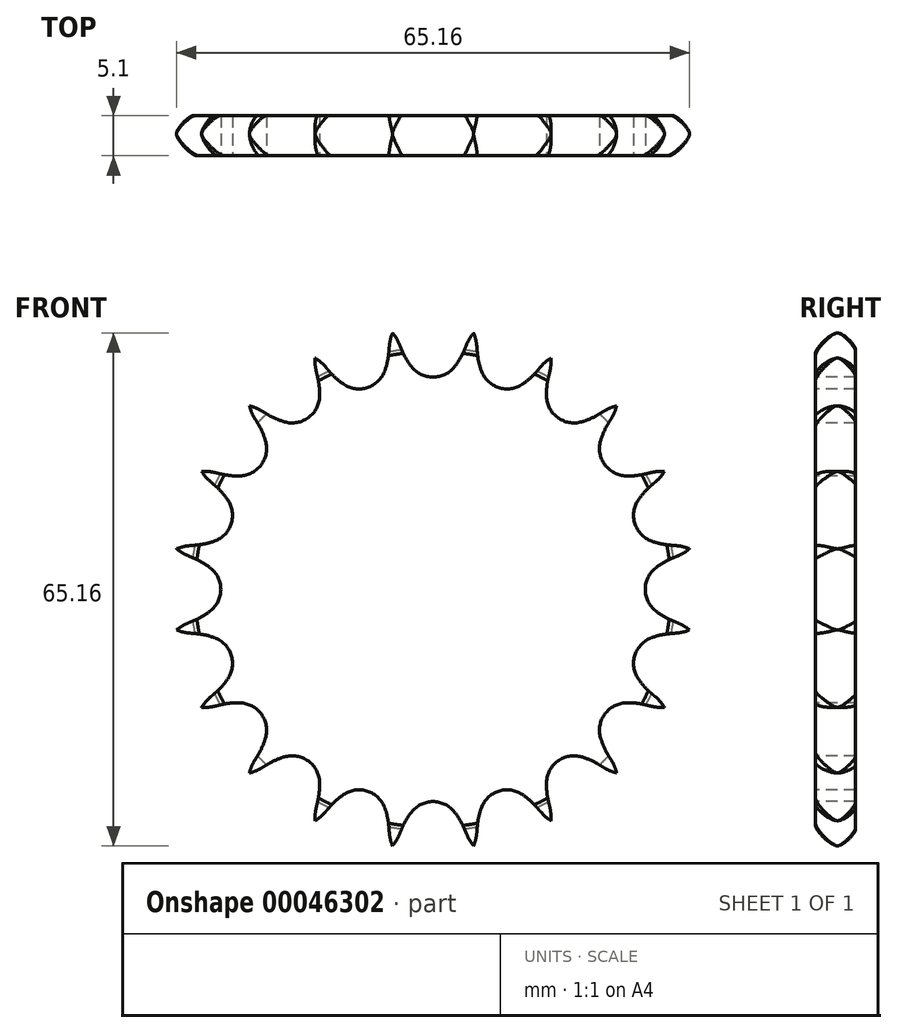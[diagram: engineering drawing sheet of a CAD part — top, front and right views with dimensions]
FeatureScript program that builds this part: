
annotation { "Feature Type Name" : "Feature", "Feature Type Description" : "" }
export const myFeature = defineFeature(function(context is Context, id is Id, definition is map)
    precondition{}
    {
        {
            var Q0;
            Q0=qCreatedBy(makeId("Right.planeOp"),FACE);
            var sketch = newSketch(context, id + "F0", { "sketchPlane" : qUnion([Q0])});
            skLineSegment(sketch, "E0", {"start": v(0, 0) * mm, "end": v(5.1, 0) * mm, "construction": true});
            skLineSegment(sketch, "E1", {"start": v(0, 32.98) * mm, "end": v(5.1, 32.98) * mm});
            skLineSegment(sketch, "E2", {"start": v(5.1, 32.98) * mm, "end": v(5.1, 30) * mm});
            skLineSegment(sketch, "E3", {"start": v(5.1, 30) * mm, "end": v(5.1, 30) * mm});
            skLineSegment(sketch, "E4", {"start": v(5.1, 30) * mm, "end": v(5.1, 0) * mm});
            skLineSegment(sketch, "E5", {"start": v(0, 0) * mm, "end": v(0, 32.98) * mm});
            skLineSegment(sketch, "E6.0.MirrorCS", {"start": v(0, -32.98) * mm, "end": v(5.1, -32.98) * mm});
            skLineSegment(sketch, "E6.1.MirrorCS", {"start": v(5.1, -32.98) * mm, "end": v(5.1, -30) * mm});
            skLineSegment(sketch, "E6.3.MirrorCS", {"start": v(5.1, -30) * mm, "end": v(5.1, 0) * mm});
            skLineSegment(sketch, "E6.4.MirrorCS", {"start": v(5.1, -30) * mm, "end": v(5.1, -30) * mm});
            skLineSegment(sketch, "E6.5.MirrorCS", {"start": v(0, 0) * mm, "end": v(0, -32.98) * mm});
            skLineSegment(sketch, "E7", {"start": v(0, 0) * mm, "end": v(5.1, 0) * mm});
            skLineSegment(sketch, "E8", {"start": v(5.1, 30) * mm, "end": v(0, 30) * mm, "construction": true});
            skLineSegment(sketch, "E9", {"start": v(5.1, -30) * mm, "end": v(0, -30) * mm, "construction": true});
            skSolve(sketch);
        }
        {
            var Q0;
            Q0=makeQuery(id+"F0.imprint","IMPRINT",FACE,{"disambiguationData":[TD([[makeQuery(id+"F0.imprint","IMPRINT",EDGE,{"derivedFrom":sQuery(id+"F0.wireOp",EDGE,"E1")}),-1.0]])]});
            var Q1;
            Q1=sQuery(id+"F0.wireOp",EDGE,"E0");
            revolve(context, id + "F1", {"entities" : qUnion([Q0]), "axis" : qUnion([Q1]), "revolveType" : RevolveType.FULL});
        }
        {
            var Q0;
            Q0=makeQuery(id+"F1.opRevolve","SWEPT_EDGE",EDGE,{"disambiguationData":[OSD([sQuery(id+"F0.wireOp",EDGE,"E1"),sQuery(id+"F0.wireOp",EDGE,"E5")])]});
            fillet(context, id + "F2", {"entities" : qUnion([Q0]), "radius" : 2.75 * mm, "tangentPropagation" : true, "rho" : 0.2, "crossSection" : FilletCrossSection.CONIC, "allowEdgeOverflow" : false});
        }
        {
            var Q0;
            Q0=makeQuery(id+"F1.opRevolve","SWEPT_EDGE",EDGE,{"disambiguationData":[OSD([sQuery(id+"F0.wireOp",EDGE,"E1"),sQuery(id+"F0.wireOp",EDGE,"E2")])]});
            fillet(context, id + "F3", {"entities" : qUnion([Q0]), "radius" : 2.25 * mm, "tangentPropagation" : true, "rho" : 0.2, "crossSection" : FilletCrossSection.CONIC, "allowEdgeOverflow" : false});
        }
        {
            var Q0;
            Q0=makeQuery(id+"F1.opRevolve","SWEPT_FACE",FACE,{"disambiguationData":[OSD([sQuery(id+"F0.wireOp",EDGE,"E5")])]});
            var sketch = newSketch(context, id + "F4", { "sketchPlane" : qUnion([Q0])});
            skCircle(sketch, "E10", {"center": v(0, 0) * mm, "radius": 30.44 * mm, "construction": true});
            skLineSegment(sketch, "E11", {"start": v(0, 0) * mm, "end": v(0, 30.44) * mm, "construction": true});
            skLineSegment(sketch, "E12", {"start": v(0, 30.44) * mm, "end": v(17.07, 30.44) * mm, "construction": true});
            skLineSegment(sketch, "E13", {"start": v(0, 30.44) * mm, "end": v(4.32, 33.82) * mm, "construction": true});
            skLineSegment(sketch, "E14", {"start": v(4.32, 33.82) * mm, "end": v(-3.95, 30.35) * mm, "construction": true});
            skLineSegment(sketch, "E15", {"start": v(-3.95, 30.35) * mm, "end": v(-4.28, 31.13) * mm});
            skLineSegment(sketch, "E16", {"start": v(0, 0) * mm, "end": v(-5.16, 32.58) * mm, "construction": true});
            skArc(sketch, "E17", {"start": v(-5.16, 32.58) * mm, "mid": v(-14.3, 26) * mm, "end": v(-4.28, 31.13) * mm, "construction": true});
            skArc(sketch, "E18", {"start": v(-4.28, 31.13) * mm, "mid": v(-4.66, 31.89) * mm, "end": v(-5.16, 32.58) * mm});
            skLineSegment(sketch, "E19", {"start": v(-4.28, 31.13) * mm, "end": v(-10.5, 45.96) * mm, "construction": true});
            skArc(sketch, "E20", {"start": v(-3.95, 30.35) * mm, "mid": v(-3.41, 29.28) * mm, "end": v(-2.75, 28.3) * mm});
            skArc(sketch, "E21", {"start": v(-2.75, 28.3) * mm, "mid": v(12.06, 38.36) * mm, "end": v(-3.95, 30.35) * mm, "construction": true});
            skArc(sketch, "E22.0.MirrorCS", {"start": v(3.95, 30.35) * mm, "mid": v(3.41, 29.28) * mm, "end": v(2.75, 28.3) * mm});
            skLineSegment(sketch, "E23.0.MirrorCS", {"start": v(3.95, 30.35) * mm, "end": v(4.28, 31.13) * mm});
            skArc(sketch, "E24.0.MirrorCS", {"start": v(4.28, 31.13) * mm, "mid": v(4.66, 31.89) * mm, "end": v(5.16, 32.58) * mm});
            skArc(sketch, "E25", {"start": v(-2.75, 28.3) * mm, "mid": v(0, 26.96) * mm, "end": v(2.75, 28.3) * mm});
            skArc(sketch, "E26", {"start": v(2.75, 28.3) * mm, "mid": v(0, 33.93) * mm, "end": v(-2.75, 28.3) * mm, "construction": true});
            skLineSegment(sketch, "E27", {"start": v(-49.44, 0) * mm, "end": v(0, 0) * mm, "construction": true});
            skArc(sketch, "E28.1.0", {"start": v(-5.55, 30.93) * mm, "mid": v(-5.42, 31.77) * mm, "end": v(-5.16, 32.58) * mm});
            skLineSegment(sketch, "E28.1.1", {"start": v(-5.62, 30.08) * mm, "end": v(-5.55, 30.93) * mm});
            skArc(sketch, "E28.1.2", {"start": v(-5.62, 30.08) * mm, "mid": v(-5.8, 28.9) * mm, "end": v(-6.13, 27.76) * mm});
            skArc(sketch, "E28.1.3", {"start": v(-11.36, 26.07) * mm, "mid": v(-8.33, 25.64) * mm, "end": v(-6.13, 27.76) * mm});
            skArc(sketch, "E28.1.4", {"start": v(-13.13, 27.64) * mm, "mid": v(-12.3, 26.8) * mm, "end": v(-11.36, 26.07) * mm});
            skLineSegment(sketch, "E28.1.5", {"start": v(-13.13, 27.64) * mm, "end": v(-13.69, 28.29) * mm});
            skArc(sketch, "E28.1.6", {"start": v(-13.69, 28.29) * mm, "mid": v(-14.29, 28.89) * mm, "end": v(-14.97, 29.39) * mm});
            skArc(sketch, "E28.2.0", {"start": v(-14.84, 27.7) * mm, "mid": v(-14.97, 28.54) * mm, "end": v(-14.97, 29.39) * mm});
            skLineSegment(sketch, "E28.2.1", {"start": v(-14.64, 26.87) * mm, "end": v(-14.84, 27.7) * mm});
            skArc(sketch, "E28.2.2", {"start": v(-14.64, 26.87) * mm, "mid": v(-14.45, 25.7) * mm, "end": v(-14.41, 24.5) * mm});
            skArc(sketch, "E28.2.3", {"start": v(-18.85, 21.28) * mm, "mid": v(-15.85, 21.81) * mm, "end": v(-14.41, 24.5) * mm});
            skArc(sketch, "E28.2.4", {"start": v(-21.03, 22.23) * mm, "mid": v(-19.97, 21.68) * mm, "end": v(-18.85, 21.28) * mm});
            skLineSegment(sketch, "E28.2.5", {"start": v(-21.03, 22.23) * mm, "end": v(-21.76, 22.67) * mm});
            skArc(sketch, "E28.2.6", {"start": v(-21.76, 22.67) * mm, "mid": v(-22.52, 23.06) * mm, "end": v(-23.32, 23.32) * mm});
            skArc(sketch, "E28.3.0", {"start": v(-22.67, 21.76) * mm, "mid": v(-23.06, 22.52) * mm, "end": v(-23.32, 23.32) * mm});
            skLineSegment(sketch, "E28.3.1", {"start": v(-22.23, 21.03) * mm, "end": v(-22.67, 21.76) * mm});
            skArc(sketch, "E28.3.2", {"start": v(-22.23, 21.03) * mm, "mid": v(-21.68, 19.97) * mm, "end": v(-21.28, 18.85) * mm});
            skArc(sketch, "E28.3.3", {"start": v(-24.5, 14.41) * mm, "mid": v(-21.81, 15.85) * mm, "end": v(-21.28, 18.85) * mm});
            skArc(sketch, "E28.3.4", {"start": v(-26.87, 14.64) * mm, "mid": v(-25.7, 14.45) * mm, "end": v(-24.5, 14.41) * mm});
            skLineSegment(sketch, "E28.3.5", {"start": v(-26.87, 14.64) * mm, "end": v(-27.7, 14.84) * mm});
            skArc(sketch, "E28.3.6", {"start": v(-27.7, 14.84) * mm, "mid": v(-28.54, 14.97) * mm, "end": v(-29.39, 14.97) * mm});
            skArc(sketch, "E28.4.0", {"start": v(-28.29, 13.69) * mm, "mid": v(-28.89, 14.29) * mm, "end": v(-29.39, 14.97) * mm});
            skLineSegment(sketch, "E28.4.1", {"start": v(-27.64, 13.13) * mm, "end": v(-28.29, 13.69) * mm});
            skArc(sketch, "E28.4.2", {"start": v(-27.64, 13.13) * mm, "mid": v(-26.8, 12.3) * mm, "end": v(-26.07, 11.36) * mm});
            skArc(sketch, "E28.4.3", {"start": v(-27.76, 6.13) * mm, "mid": v(-25.64, 8.33) * mm, "end": v(-26.07, 11.36) * mm});
            skArc(sketch, "E28.4.4", {"start": v(-30.08, 5.62) * mm, "mid": v(-28.9, 5.8) * mm, "end": v(-27.76, 6.13) * mm});
            skLineSegment(sketch, "E28.4.5", {"start": v(-30.08, 5.62) * mm, "end": v(-30.93, 5.55) * mm});
            skArc(sketch, "E28.4.6", {"start": v(-30.93, 5.55) * mm, "mid": v(-31.77, 5.42) * mm, "end": v(-32.58, 5.16) * mm});
            skArc(sketch, "E28.5.0", {"start": v(-31.13, 4.28) * mm, "mid": v(-31.89, 4.66) * mm, "end": v(-32.58, 5.16) * mm});
            skLineSegment(sketch, "E28.5.1", {"start": v(-30.35, 3.95) * mm, "end": v(-31.13, 4.28) * mm});
            skArc(sketch, "E28.5.2", {"start": v(-30.35, 3.95) * mm, "mid": v(-29.28, 3.41) * mm, "end": v(-28.3, 2.75) * mm});
            skArc(sketch, "E28.5.3", {"start": v(-28.3, -2.75) * mm, "mid": v(-26.96, 0) * mm, "end": v(-28.3, 2.75) * mm});
            skArc(sketch, "E28.5.4", {"start": v(-30.35, -3.95) * mm, "mid": v(-29.28, -3.41) * mm, "end": v(-28.3, -2.75) * mm});
            skLineSegment(sketch, "E28.5.5", {"start": v(-30.35, -3.95) * mm, "end": v(-31.13, -4.28) * mm});
            skArc(sketch, "E28.5.6", {"start": v(-31.13, -4.28) * mm, "mid": v(-31.89, -4.66) * mm, "end": v(-32.58, -5.16) * mm});
            skArc(sketch, "E28.6.0", {"start": v(-30.93, -5.55) * mm, "mid": v(-31.77, -5.42) * mm, "end": v(-32.58, -5.16) * mm});
            skLineSegment(sketch, "E28.6.1", {"start": v(-30.08, -5.62) * mm, "end": v(-30.93, -5.55) * mm});
            skArc(sketch, "E28.6.2", {"start": v(-30.08, -5.62) * mm, "mid": v(-28.9, -5.8) * mm, "end": v(-27.76, -6.13) * mm});
            skArc(sketch, "E28.6.3", {"start": v(-26.07, -11.36) * mm, "mid": v(-25.64, -8.33) * mm, "end": v(-27.76, -6.13) * mm});
            skArc(sketch, "E28.6.4", {"start": v(-27.64, -13.13) * mm, "mid": v(-26.8, -12.3) * mm, "end": v(-26.07, -11.36) * mm});
            skLineSegment(sketch, "E28.6.5", {"start": v(-27.64, -13.13) * mm, "end": v(-28.29, -13.69) * mm});
            skArc(sketch, "E28.6.6", {"start": v(-28.29, -13.69) * mm, "mid": v(-28.89, -14.29) * mm, "end": v(-29.39, -14.97) * mm});
            skArc(sketch, "E28.7.0", {"start": v(-27.7, -14.84) * mm, "mid": v(-28.54, -14.97) * mm, "end": v(-29.39, -14.97) * mm});
            skLineSegment(sketch, "E28.7.1", {"start": v(-26.87, -14.64) * mm, "end": v(-27.7, -14.84) * mm});
            skArc(sketch, "E28.7.2", {"start": v(-26.87, -14.64) * mm, "mid": v(-25.7, -14.45) * mm, "end": v(-24.5, -14.41) * mm});
            skArc(sketch, "E28.7.3", {"start": v(-21.28, -18.85) * mm, "mid": v(-21.81, -15.85) * mm, "end": v(-24.5, -14.41) * mm});
            skArc(sketch, "E28.7.4", {"start": v(-22.23, -21.03) * mm, "mid": v(-21.68, -19.97) * mm, "end": v(-21.28, -18.85) * mm});
            skLineSegment(sketch, "E28.7.5", {"start": v(-22.23, -21.03) * mm, "end": v(-22.67, -21.76) * mm});
            skArc(sketch, "E28.7.6", {"start": v(-22.67, -21.76) * mm, "mid": v(-23.06, -22.52) * mm, "end": v(-23.32, -23.32) * mm});
            skArc(sketch, "E28.8.0", {"start": v(-21.76, -22.67) * mm, "mid": v(-22.52, -23.06) * mm, "end": v(-23.32, -23.32) * mm});
            skLineSegment(sketch, "E28.8.1", {"start": v(-21.03, -22.23) * mm, "end": v(-21.76, -22.67) * mm});
            skArc(sketch, "E28.8.2", {"start": v(-21.03, -22.23) * mm, "mid": v(-19.97, -21.68) * mm, "end": v(-18.85, -21.28) * mm});
            skArc(sketch, "E28.8.3", {"start": v(-14.41, -24.5) * mm, "mid": v(-15.85, -21.81) * mm, "end": v(-18.85, -21.28) * mm});
            skArc(sketch, "E28.8.4", {"start": v(-14.64, -26.87) * mm, "mid": v(-14.45, -25.7) * mm, "end": v(-14.41, -24.5) * mm});
            skLineSegment(sketch, "E28.8.5", {"start": v(-14.64, -26.87) * mm, "end": v(-14.84, -27.7) * mm});
            skArc(sketch, "E28.8.6", {"start": v(-14.84, -27.7) * mm, "mid": v(-14.97, -28.54) * mm, "end": v(-14.97, -29.39) * mm});
            skArc(sketch, "E28.9.0", {"start": v(-13.69, -28.29) * mm, "mid": v(-14.29, -28.89) * mm, "end": v(-14.97, -29.39) * mm});
            skLineSegment(sketch, "E28.9.1", {"start": v(-13.13, -27.64) * mm, "end": v(-13.69, -28.29) * mm});
            skArc(sketch, "E28.9.2", {"start": v(-13.13, -27.64) * mm, "mid": v(-12.3, -26.8) * mm, "end": v(-11.36, -26.07) * mm});
            skArc(sketch, "E28.9.3", {"start": v(-6.13, -27.76) * mm, "mid": v(-8.33, -25.64) * mm, "end": v(-11.36, -26.07) * mm});
            skArc(sketch, "E28.9.4", {"start": v(-5.62, -30.08) * mm, "mid": v(-5.8, -28.9) * mm, "end": v(-6.13, -27.76) * mm});
            skLineSegment(sketch, "E28.9.5", {"start": v(-5.62, -30.08) * mm, "end": v(-5.55, -30.93) * mm});
            skArc(sketch, "E28.9.6", {"start": v(-5.55, -30.93) * mm, "mid": v(-5.42, -31.77) * mm, "end": v(-5.16, -32.58) * mm});
            skArc(sketch, "E28.10.0", {"start": v(-4.28, -31.13) * mm, "mid": v(-4.66, -31.89) * mm, "end": v(-5.16, -32.58) * mm});
            skLineSegment(sketch, "E28.10.1", {"start": v(-3.95, -30.35) * mm, "end": v(-4.28, -31.13) * mm});
            skArc(sketch, "E28.10.2", {"start": v(-3.95, -30.35) * mm, "mid": v(-3.41, -29.28) * mm, "end": v(-2.75, -28.3) * mm});
            skArc(sketch, "E28.10.3", {"start": v(2.75, -28.3) * mm, "mid": v(0, -26.96) * mm, "end": v(-2.75, -28.3) * mm});
            skArc(sketch, "E28.10.4", {"start": v(3.95, -30.35) * mm, "mid": v(3.41, -29.28) * mm, "end": v(2.75, -28.3) * mm});
            skLineSegment(sketch, "E28.10.5", {"start": v(3.95, -30.35) * mm, "end": v(4.28, -31.13) * mm});
            skArc(sketch, "E28.10.6", {"start": v(4.28, -31.13) * mm, "mid": v(4.66, -31.89) * mm, "end": v(5.16, -32.58) * mm});
            skArc(sketch, "E28.11.0", {"start": v(5.55, -30.93) * mm, "mid": v(5.42, -31.77) * mm, "end": v(5.16, -32.58) * mm});
            skLineSegment(sketch, "E28.11.1", {"start": v(5.62, -30.08) * mm, "end": v(5.55, -30.93) * mm});
            skArc(sketch, "E28.11.2", {"start": v(5.62, -30.08) * mm, "mid": v(5.8, -28.9) * mm, "end": v(6.13, -27.76) * mm});
            skArc(sketch, "E28.11.3", {"start": v(11.36, -26.07) * mm, "mid": v(8.33, -25.64) * mm, "end": v(6.13, -27.76) * mm});
            skArc(sketch, "E28.11.4", {"start": v(13.13, -27.64) * mm, "mid": v(12.3, -26.8) * mm, "end": v(11.36, -26.07) * mm});
            skLineSegment(sketch, "E28.11.5", {"start": v(13.13, -27.64) * mm, "end": v(13.69, -28.29) * mm});
            skArc(sketch, "E28.11.6", {"start": v(13.69, -28.29) * mm, "mid": v(14.29, -28.89) * mm, "end": v(14.97, -29.39) * mm});
            skArc(sketch, "E28.12.0", {"start": v(14.84, -27.7) * mm, "mid": v(14.97, -28.54) * mm, "end": v(14.97, -29.39) * mm});
            skLineSegment(sketch, "E28.12.1", {"start": v(14.64, -26.87) * mm, "end": v(14.84, -27.7) * mm});
            skArc(sketch, "E28.12.2", {"start": v(14.64, -26.87) * mm, "mid": v(14.45, -25.7) * mm, "end": v(14.41, -24.5) * mm});
            skArc(sketch, "E28.12.3", {"start": v(18.85, -21.28) * mm, "mid": v(15.85, -21.81) * mm, "end": v(14.41, -24.5) * mm});
            skArc(sketch, "E28.12.4", {"start": v(21.03, -22.23) * mm, "mid": v(19.97, -21.68) * mm, "end": v(18.85, -21.28) * mm});
            skLineSegment(sketch, "E28.12.5", {"start": v(21.03, -22.23) * mm, "end": v(21.76, -22.67) * mm});
            skArc(sketch, "E28.12.6", {"start": v(21.76, -22.67) * mm, "mid": v(22.52, -23.06) * mm, "end": v(23.32, -23.32) * mm});
            skArc(sketch, "E28.13.0", {"start": v(22.67, -21.76) * mm, "mid": v(23.06, -22.52) * mm, "end": v(23.32, -23.32) * mm});
            skLineSegment(sketch, "E28.13.1", {"start": v(22.23, -21.03) * mm, "end": v(22.67, -21.76) * mm});
            skArc(sketch, "E28.13.2", {"start": v(22.23, -21.03) * mm, "mid": v(21.68, -19.97) * mm, "end": v(21.28, -18.85) * mm});
            skArc(sketch, "E28.13.3", {"start": v(24.5, -14.41) * mm, "mid": v(21.81, -15.85) * mm, "end": v(21.28, -18.85) * mm});
            skArc(sketch, "E28.13.4", {"start": v(26.87, -14.64) * mm, "mid": v(25.7, -14.45) * mm, "end": v(24.5, -14.41) * mm});
            skLineSegment(sketch, "E28.13.5", {"start": v(26.87, -14.64) * mm, "end": v(27.7, -14.84) * mm});
            skArc(sketch, "E28.13.6", {"start": v(27.7, -14.84) * mm, "mid": v(28.54, -14.97) * mm, "end": v(29.39, -14.97) * mm});
            skArc(sketch, "E28.14.0", {"start": v(28.29, -13.69) * mm, "mid": v(28.89, -14.29) * mm, "end": v(29.39, -14.97) * mm});
            skLineSegment(sketch, "E28.14.1", {"start": v(27.64, -13.13) * mm, "end": v(28.29, -13.69) * mm});
            skArc(sketch, "E28.14.2", {"start": v(27.64, -13.13) * mm, "mid": v(26.8, -12.3) * mm, "end": v(26.07, -11.36) * mm});
            skArc(sketch, "E28.14.3", {"start": v(27.76, -6.13) * mm, "mid": v(25.64, -8.33) * mm, "end": v(26.07, -11.36) * mm});
            skArc(sketch, "E28.14.4", {"start": v(30.08, -5.62) * mm, "mid": v(28.9, -5.8) * mm, "end": v(27.76, -6.13) * mm});
            skLineSegment(sketch, "E28.14.5", {"start": v(30.08, -5.62) * mm, "end": v(30.93, -5.55) * mm});
            skArc(sketch, "E28.14.6", {"start": v(30.93, -5.55) * mm, "mid": v(31.77, -5.42) * mm, "end": v(32.58, -5.16) * mm});
            skArc(sketch, "E28.15.0", {"start": v(31.13, -4.28) * mm, "mid": v(31.89, -4.66) * mm, "end": v(32.58, -5.16) * mm});
            skLineSegment(sketch, "E28.15.1", {"start": v(30.35, -3.95) * mm, "end": v(31.13, -4.28) * mm});
            skArc(sketch, "E28.15.2", {"start": v(30.35, -3.95) * mm, "mid": v(29.28, -3.41) * mm, "end": v(28.3, -2.75) * mm});
            skArc(sketch, "E28.15.3", {"start": v(28.3, 2.75) * mm, "mid": v(26.96, 0) * mm, "end": v(28.3, -2.75) * mm});
            skArc(sketch, "E28.15.4", {"start": v(30.35, 3.95) * mm, "mid": v(29.28, 3.41) * mm, "end": v(28.3, 2.75) * mm});
            skLineSegment(sketch, "E28.15.5", {"start": v(30.35, 3.95) * mm, "end": v(31.13, 4.28) * mm});
            skArc(sketch, "E28.15.6", {"start": v(31.13, 4.28) * mm, "mid": v(31.89, 4.66) * mm, "end": v(32.58, 5.16) * mm});
            skArc(sketch, "E28.16.0", {"start": v(30.93, 5.55) * mm, "mid": v(31.77, 5.42) * mm, "end": v(32.58, 5.16) * mm});
            skLineSegment(sketch, "E28.16.1", {"start": v(30.08, 5.62) * mm, "end": v(30.93, 5.55) * mm});
            skArc(sketch, "E28.16.2", {"start": v(30.08, 5.62) * mm, "mid": v(28.9, 5.8) * mm, "end": v(27.76, 6.13) * mm});
            skArc(sketch, "E28.16.3", {"start": v(26.07, 11.36) * mm, "mid": v(25.64, 8.33) * mm, "end": v(27.76, 6.13) * mm});
            skArc(sketch, "E28.16.4", {"start": v(27.64, 13.13) * mm, "mid": v(26.8, 12.3) * mm, "end": v(26.07, 11.36) * mm});
            skLineSegment(sketch, "E28.16.5", {"start": v(27.64, 13.13) * mm, "end": v(28.29, 13.69) * mm});
            skArc(sketch, "E28.16.6", {"start": v(28.29, 13.69) * mm, "mid": v(28.89, 14.29) * mm, "end": v(29.39, 14.97) * mm});
            skArc(sketch, "E28.17.0", {"start": v(27.7, 14.84) * mm, "mid": v(28.54, 14.97) * mm, "end": v(29.39, 14.97) * mm});
            skLineSegment(sketch, "E28.17.1", {"start": v(26.87, 14.64) * mm, "end": v(27.7, 14.84) * mm});
            skArc(sketch, "E28.17.2", {"start": v(26.87, 14.64) * mm, "mid": v(25.7, 14.45) * mm, "end": v(24.5, 14.41) * mm});
            skArc(sketch, "E28.17.3", {"start": v(21.28, 18.85) * mm, "mid": v(21.81, 15.85) * mm, "end": v(24.5, 14.41) * mm});
            skArc(sketch, "E28.17.4", {"start": v(22.23, 21.03) * mm, "mid": v(21.68, 19.97) * mm, "end": v(21.28, 18.85) * mm});
            skLineSegment(sketch, "E28.17.5", {"start": v(22.23, 21.03) * mm, "end": v(22.67, 21.76) * mm});
            skArc(sketch, "E28.17.6", {"start": v(22.67, 21.76) * mm, "mid": v(23.06, 22.52) * mm, "end": v(23.32, 23.32) * mm});
            skArc(sketch, "E28.18.0", {"start": v(21.76, 22.67) * mm, "mid": v(22.52, 23.06) * mm, "end": v(23.32, 23.32) * mm});
            skLineSegment(sketch, "E28.18.1", {"start": v(21.03, 22.23) * mm, "end": v(21.76, 22.67) * mm});
            skArc(sketch, "E28.18.2", {"start": v(21.03, 22.23) * mm, "mid": v(19.97, 21.68) * mm, "end": v(18.85, 21.28) * mm});
            skArc(sketch, "E28.18.3", {"start": v(14.41, 24.5) * mm, "mid": v(15.85, 21.81) * mm, "end": v(18.85, 21.28) * mm});
            skArc(sketch, "E28.18.4", {"start": v(14.64, 26.87) * mm, "mid": v(14.45, 25.7) * mm, "end": v(14.41, 24.5) * mm});
            skLineSegment(sketch, "E28.18.5", {"start": v(14.64, 26.87) * mm, "end": v(14.84, 27.7) * mm});
            skArc(sketch, "E28.18.6", {"start": v(14.84, 27.7) * mm, "mid": v(14.97, 28.54) * mm, "end": v(14.97, 29.39) * mm});
            skArc(sketch, "E28.19.0", {"start": v(13.69, 28.29) * mm, "mid": v(14.29, 28.89) * mm, "end": v(14.97, 29.39) * mm});
            skLineSegment(sketch, "E28.19.1", {"start": v(13.13, 27.64) * mm, "end": v(13.69, 28.29) * mm});
            skArc(sketch, "E28.19.2", {"start": v(13.13, 27.64) * mm, "mid": v(12.3, 26.8) * mm, "end": v(11.36, 26.07) * mm});
            skArc(sketch, "E28.19.3", {"start": v(6.13, 27.76) * mm, "mid": v(8.33, 25.64) * mm, "end": v(11.36, 26.07) * mm});
            skArc(sketch, "E28.19.4", {"start": v(5.62, 30.08) * mm, "mid": v(5.8, 28.9) * mm, "end": v(6.13, 27.76) * mm});
            skLineSegment(sketch, "E28.19.5", {"start": v(5.62, 30.08) * mm, "end": v(5.55, 30.93) * mm});
            skArc(sketch, "E28.19.6", {"start": v(5.55, 30.93) * mm, "mid": v(5.42, 31.77) * mm, "end": v(5.16, 32.58) * mm});
            skSolve(sketch);
        }
        {
            var Q0;
            Q0 = qSketchRegion(id + "F4", true);
            extrude(context, id + "F5", {"entities" : qUnion([Q0]), "operationType" : NewBodyOperationType.INTERSECT, "endBound" : BoundingType.THROUGH_ALL, "oppositeDirection" : true, "depth" : 25.4 * mm});
        }
    });
